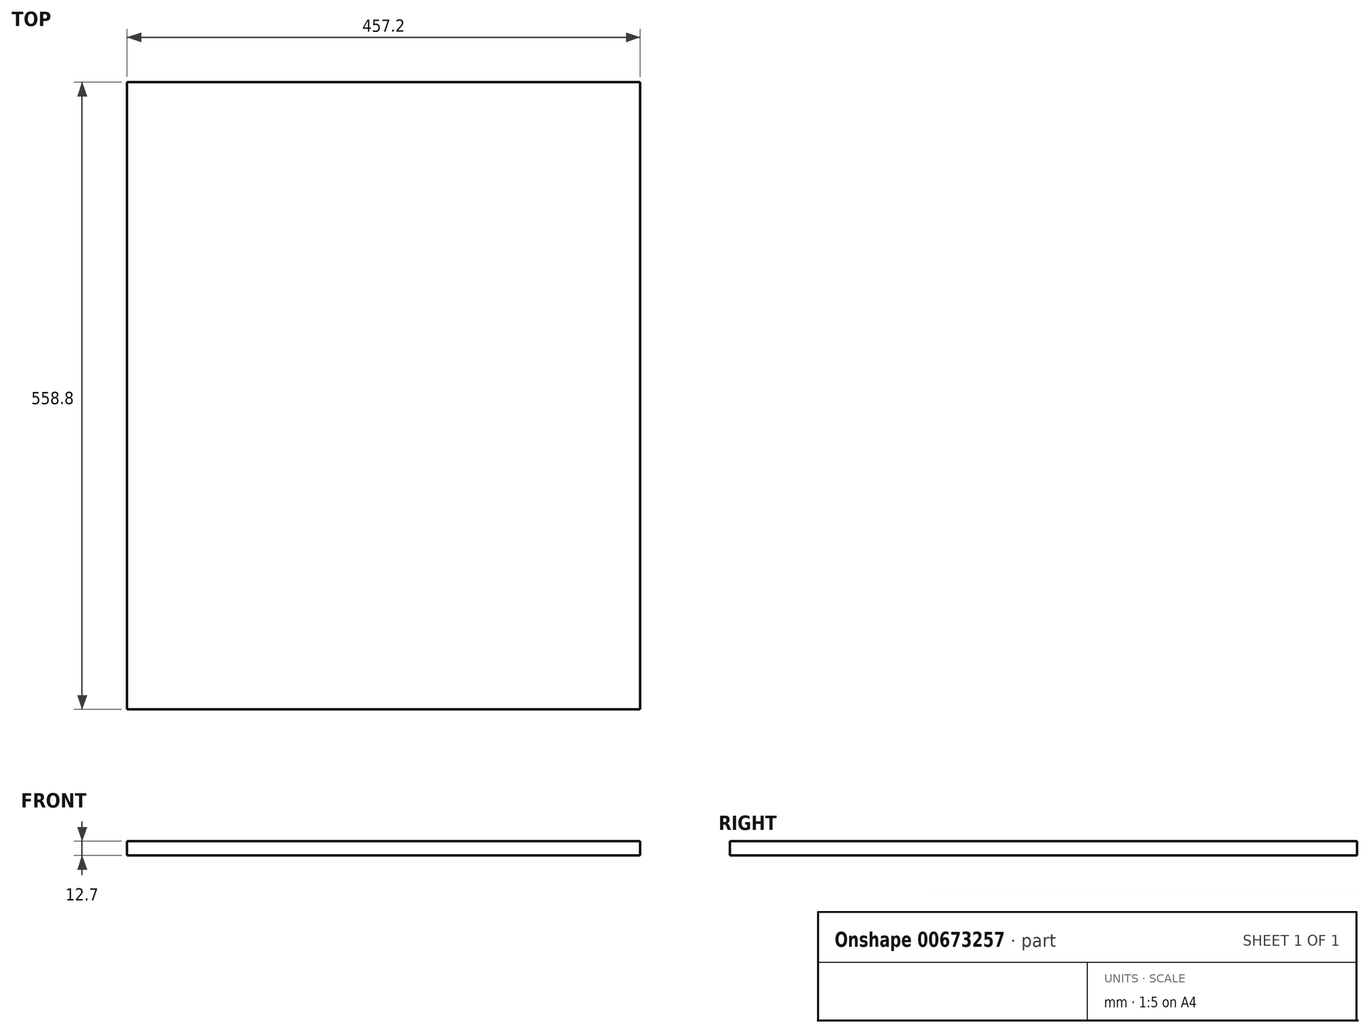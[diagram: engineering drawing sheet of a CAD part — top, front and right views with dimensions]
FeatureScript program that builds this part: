
annotation { "Feature Type Name" : "Feature", "Feature Type Description" : "" }
export const myFeature = defineFeature(function(context is Context, id is Id, definition is map)
    precondition{}
    {
        {
            var Q0;
            Q0=qCreatedBy(makeId("Top.planeOp"),FACE);
            var sketch = newSketch(context, id + "F0", { "sketchPlane" : qUnion([Q0])});
            skLineSegment(sketch, "E0.bottom", {"start": v(228.6, 279.4) * mm, "end": v(-228.6, 279.4) * mm});
            skLineSegment(sketch, "E0.top", {"start": v(228.6, -279.4) * mm, "end": v(-228.6, -279.4) * mm});
            skLineSegment(sketch, "E0.left", {"start": v(228.6, 279.4) * mm, "end": v(228.6, -279.4) * mm});
            skLineSegment(sketch, "E0.right", {"start": v(-228.6, 279.4) * mm, "end": v(-228.6, -279.4) * mm});
            skPoint(sketch, "E0.middle", {"position": v(0, 0) * mm});
            skSolve(sketch);
        }
        {
            var Q0;
            Q0=makeQuery(id+"F0.imprint","IMPRINT",FACE,{"disambiguationData":[TD([[makeQuery(id+"F0.imprint","IMPRINT",EDGE,{"derivedFrom":sQuery(id+"F0.wireOp",EDGE,"E0.bottom")}),1.0]])]});
            extrude(context, id + "F1", {"entities" : qUnion([Q0]), "depth" : 12.7 * mm, "offsetDistance" : 25.4 * mm});
        }
    });
